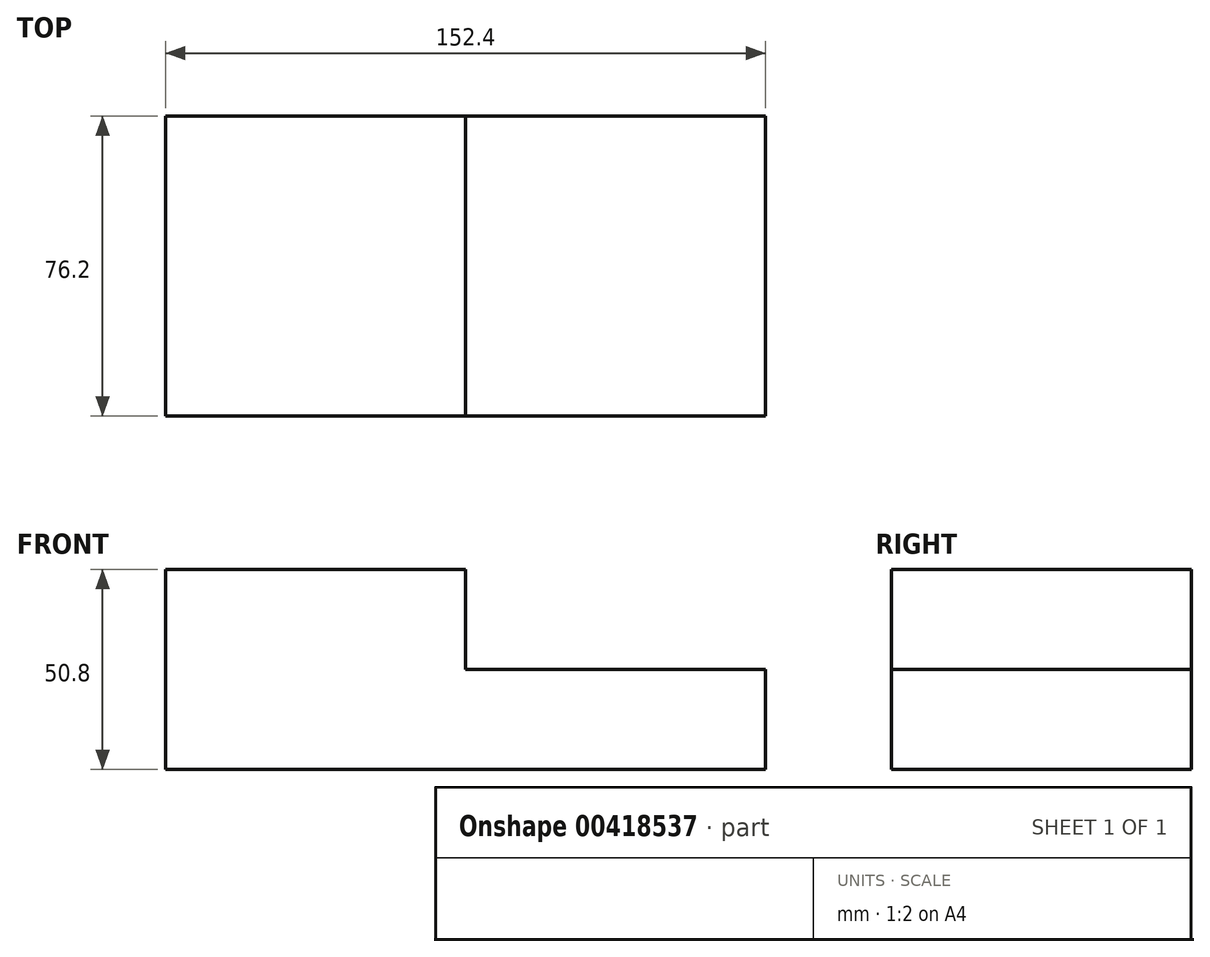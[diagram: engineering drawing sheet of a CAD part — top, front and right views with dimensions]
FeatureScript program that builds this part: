
annotation { "Feature Type Name" : "Feature", "Feature Type Description" : "" }
export const myFeature = defineFeature(function(context is Context, id is Id, definition is map)
    precondition{}
    {
        {
            var Q0;
            Q0=qCreatedBy(makeId("Front.planeOp"),FACE);
            var sketch = newSketch(context, id + "F0", { "sketchPlane" : qUnion([Q0])});
            skLineSegment(sketch, "E0", {"start": v(0, 0) * mm, "end": v(152.4, 0) * mm});
            skLineSegment(sketch, "E1", {"start": v(152.4, 0) * mm, "end": v(152.4, 25.4) * mm});
            skLineSegment(sketch, "E2", {"start": v(152.4, 25.4) * mm, "end": v(76.2, 25.4) * mm});
            skLineSegment(sketch, "E3", {"start": v(76.2, 25.4) * mm, "end": v(76.2, 50.8) * mm});
            skLineSegment(sketch, "E4", {"start": v(76.2, 50.8) * mm, "end": v(0, 50.8) * mm});
            skLineSegment(sketch, "E5", {"start": v(0, 50.8) * mm, "end": v(0, 0) * mm});
            skLineSegment(sketch, "E6", {"start": v(0, 0) * mm, "end": v(0, 50.8) * mm});
            skSolve(sketch);
        }
        {
            var Q0;
            Q0=makeQuery(id+"F0.imprint","IMPRINT",FACE,{"disambiguationData":[TD([[makeQuery(id+"F0.imprint","IMPRINT",EDGE,{"derivedFrom":sQuery(id+"F0.wireOp",EDGE,"E0")}),1.0]])]});
            extrude(context, id + "F1", {"entities" : qUnion([Q0]), "depth" : 76.2 * mm});
        }
    });
